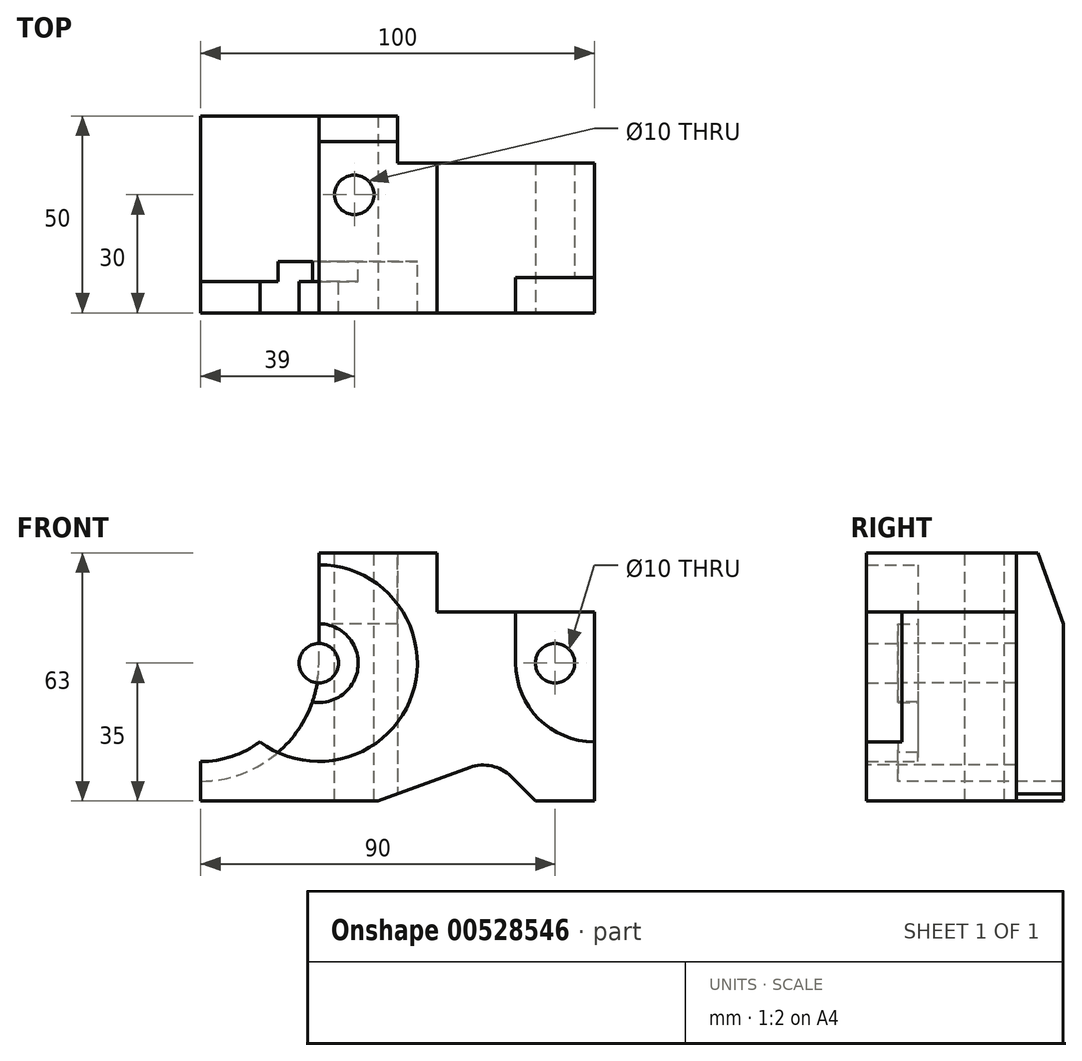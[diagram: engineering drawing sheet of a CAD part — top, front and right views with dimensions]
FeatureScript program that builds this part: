
annotation { "Feature Type Name" : "Feature", "Feature Type Description" : "" }
export const myFeature = defineFeature(function(context is Context, id is Id, definition is map)
    precondition{}
    {
        {
            var Q0;
            Q0=qCreatedBy(makeId("Front.planeOp"),FACE);
            var sketch = newSketch(context, id + "F0", { "sketchPlane" : qUnion([Q0])});
            skLineSegment(sketch, "E0", {"start": v(0, 0) * mm, "end": v(-15, 0) * mm});
            skLineSegment(sketch, "E1", {"start": v(-100, 0) * mm, "end": v(-100, 63) * mm});
            skLineSegment(sketch, "E2", {"start": v(-100, 63) * mm, "end": v(-40, 63) * mm});
            skLineSegment(sketch, "E3", {"start": v(-40, 63) * mm, "end": v(-40, 48) * mm});
            skLineSegment(sketch, "E4", {"start": v(-40, 48) * mm, "end": v(0, 48) * mm});
            skLineSegment(sketch, "E5", {"start": v(0, 48) * mm, "end": v(0, 0) * mm});
            skLineSegment(sketch, "E6", {"start": v(-15, 0) * mm, "end": v(-21.17, 6.17) * mm});
            skArc(sketch, "E7", {"start": v(-21.17, 6.17) * mm, "mid": v(-26.08, 8.86) * mm, "end": v(-31.66, 8.5) * mm});
            skLineSegment(sketch, "E8", {"start": v(-31.66, 8.5) * mm, "end": v(-55, 0) * mm});
            skLineSegment(sketch, "E9.trimOffspring", {"start": v(-55, 0) * mm, "end": v(-100, 0) * mm});
            skSolve(sketch);
        }
        {
            var Q0;
            Q0 = qSketchRegion(id + "F0", true);
            extrude(context, id + "F1", {"entities" : qUnion([Q0]), "oppositeDirection" : true, "depth" : 50 * mm, "offsetDistance" : 25 * mm});
        }
        {
            var Q0;
            Q0=qCreatedBy(makeId("Top.planeOp"),FACE);
            cPlane(context, id + "F2", {"entities" : qUnion([Q0]), "cplaneType" : CPlaneType.OFFSET, "offset" : 35 * mm, "width" : 150 * mm, "height" : 150 * mm});
        }
        {
            var Q0;
            Q0=qCreatedBy(id+"F2.planeOp",FACE);
            var sketch = newSketch(context, id + "F3", { "sketchPlane" : qUnion([Q0])});
            skLineSegment(sketch, "E10", {"start": v(-70, -45.38) * mm, "end": v(-70, 0) * mm});
            skLineSegment(sketch, "E11", {"start": v(-70, 0) * mm, "end": v(-75, 0) * mm});
            skLineSegment(sketch, "E12", {"start": v(-75, 0) * mm, "end": v(-75, 8) * mm});
            skLineSegment(sketch, "E13", {"start": v(-75, 8) * mm, "end": v(-80, 8) * mm});
            skLineSegment(sketch, "E14", {"start": v(-95, 13) * mm, "end": v(-95, -45.38) * mm});
            skLineSegment(sketch, "E15", {"start": v(-95, -45.38) * mm, "end": v(-70, -45.38) * mm});
            skLineSegment(sketch, "E16", {"start": v(-80, 8) * mm, "end": v(-80, 13) * mm});
            skLineSegment(sketch, "E17", {"start": v(-80, 13) * mm, "end": v(-95, 13) * mm});
            skLineSegment(sketch, "E18", {"start": v(-70, 0) * mm, "end": v(-70, 92.14) * mm, "construction": true});
            skSolve(sketch);
        }
        {
            var Q0;
            Q0=makeQuery(id+"F3.imprint","IMPRINT",FACE,{"disambiguationData":[TD([[makeQuery(id+"F3.imprint","IMPRINT",EDGE,{"derivedFrom":sQuery(id+"F3.wireOp",EDGE,"E10")}),1.0]])]});
            var Q1;
            Q1=sQuery(id+"F3.wireOp",EDGE,"E18");
            revolve(context, id + "F4", {"operationType" : NewBodyOperationType.REMOVE, "entities" : qUnion([Q0]), "axis" : qUnion([Q1]), "revolveType" : RevolveType.FULL, "oppositeDirection" : true});
        }
        {
            var Q0;
            Q0=qCreatedBy(makeId("Front.planeOp"),FACE);
            var sketch = newSketch(context, id + "F5", { "sketchPlane" : qUnion([Q0])});
            skLineSegment(sketch, "E19", {"start": v(-20, 71.47) * mm, "end": v(-20, 35) * mm});
            skArc(sketch, "E20", {"start": v(-20, 35) * mm, "mid": v(-14.14, 20.86) * mm, "end": v(0, 15) * mm});
            skLineSegment(sketch, "E21", {"start": v(0, 15) * mm, "end": v(24.4, 15) * mm});
            skLineSegment(sketch, "E22", {"start": v(-20, 71.47) * mm, "end": v(24.4, 71.47) * mm});
            skLineSegment(sketch, "E23", {"start": v(24.4, 71.47) * mm, "end": v(24.4, 15) * mm});
            skCircle(sketch, "E24.0.0", {"center": v(-70, 35) * mm, "radius": 5 * mm, "construction": true});
            skLineSegment(sketch, "E25", {"start": v(-70, 35) * mm, "end": v(0, 35) * mm, "construction": true});
            skSolve(sketch);
        }
        {
            var Q0;
            Q0 = qSketchRegion(id + "F5", true);
            extrude(context, id + "F6", {"entities" : qUnion([Q0]), "operationType" : NewBodyOperationType.REMOVE, "oppositeDirection" : true, "depth" : 9 * mm, "offsetDistance" : 25 * mm});
        }
        {
            var Q0;
            Q0=qCreatedBy(makeId("Front.planeOp"),FACE);
            var sketch = newSketch(context, id + "F7", { "sketchPlane" : qUnion([Q0])});
            skCircle(sketch, "E26", {"center": v(-10, 35) * mm, "radius": 5 * mm});
            skSolve(sketch);
        }
        {
            var Q0;
            Q0 = qSketchRegion(id + "F7", true);
            extrude(context, id + "F8", {"entities" : qUnion([Q0]), "operationType" : NewBodyOperationType.REMOVE, "endBound" : BoundingType.THROUGH_ALL, "oppositeDirection" : true, "depth" : 25 * mm, "offsetDistance" : 25 * mm});
        }
        {
            var Q0;
            Q0=qCreatedBy(makeId("Front.planeOp"),FACE);
            cPlane(context, id + "F9", {"entities" : qUnion([Q0]), "cplaneType" : CPlaneType.OFFSET, "offset" : 8 * mm, "oppositeDirection" : true, "width" : 150 * mm, "height" : 150 * mm});
        }
        {
            var Q0;
            Q0=qCreatedBy(id+"F9.planeOp",FACE);
            var sketch = newSketch(context, id + "F10", { "sketchPlane" : qUnion([Q0])});
            skLineSegment(sketch, "E27", {"start": v(-192.21, 5) * mm, "end": v(-100, 5) * mm});
            skLineSegment(sketch, "E28", {"start": v(-70, 35) * mm, "end": v(-70, 107.14) * mm});
            skLineSegment(sketch, "E29", {"start": v(-70, 107.14) * mm, "end": v(-192.21, 107.14) * mm});
            skLineSegment(sketch, "E30", {"start": v(-192.21, 107.14) * mm, "end": v(-192.21, 5) * mm});
            skPoint(sketch, "E31.visualSharp", {"position": v(-70, 5) * mm});
            skArc(sketch, "E31.filletArc", {"start": v(-100, 5) * mm, "mid": v(-78.79, 13.79) * mm, "end": v(-70, 35) * mm});
            skSolve(sketch);
        }
        {
            var Q0;
            Q0 = qSketchRegion(id + "F10", true);
            extrude(context, id + "F11", {"entities" : qUnion([Q0]), "operationType" : NewBodyOperationType.REMOVE, "endBound" : BoundingType.THROUGH_ALL, "oppositeDirection" : true, "depth" : 25 * mm, "offsetDistance" : 25 * mm});
        }
        {
            var Q0;
            Q0=qCreatedBy(id+"F9.planeOp",FACE);
            var sketch = newSketch(context, id + "F12", { "sketchPlane" : qUnion([Q0])});
            skLineSegment(sketch, "E32", {"start": v(-100, 14.4) * mm, "end": v(-100, 35) * mm, "construction": true});
            skLineSegment(sketch, "E33", {"start": v(-100, 35) * mm, "end": v(-70, 35) * mm, "construction": true});
            skArc(sketch, "E34", {"start": v(-123.4, 26.22) * mm, "mid": v(-95.54, 10.4) * mm, "end": v(-75, 35) * mm});
            skLineSegment(sketch, "E35", {"start": v(-75, 35) * mm, "end": v(-75, 45) * mm});
            skLineSegment(sketch, "E36", {"start": v(-75, 45) * mm, "end": v(-70, 45) * mm});
            skLineSegment(sketch, "E37", {"start": v(-70, 45) * mm, "end": v(-70, 99.63) * mm});
            skLineSegment(sketch, "E38", {"start": v(-70, 99.63) * mm, "end": v(-123.4, 99.63) * mm});
            skLineSegment(sketch, "E39", {"start": v(-123.4, 99.63) * mm, "end": v(-123.4, 26.22) * mm});
            skSolve(sketch);
        }
        {
            var Q0;
            Q0 = qSketchRegion(id + "F12", true);
            extrude(context, id + "F13", {"entities" : qUnion([Q0]), "operationType" : NewBodyOperationType.REMOVE, "depth" : 25 * mm, "offsetDistance" : 25 * mm});
        }
        {
            var Q0;
            Q0=makeQuery(id+"F13.boolean.opBoolean","MERGE",FACE,{"derivedFrom":[makeQuery(id+"F11.boolean.opBoolean","COPY",FACE,{"derivedFrom":makeQuery(id+"F11.opExtrude","SWEPT_FACE",FACE,{"disambiguationData":[OSD([sQuery(id+"F10.wireOp",EDGE,"E28")])]})}),makeQuery(id+"F13.opExtrude","SWEPT_FACE",FACE,{"disambiguationData":[OSD([sQuery(id+"F12.wireOp",EDGE,"E37")])]})]});
            var sketch = newSketch(context, id + "F14", { "sketchPlane" : qUnion([Q0])});
            skLineSegment(sketch, "E40", {"start": v(-50, 63) * mm, "end": v(-50, 45) * mm});
            skLineSegment(sketch, "E41", {"start": v(-50, 45) * mm, "end": v(-43.45, 63) * mm});
            skLineSegment(sketch, "E42", {"start": v(-43.45, 63) * mm, "end": v(-50, 63) * mm});
            skSolve(sketch);
        }
        {
            var Q0;
            Q0 = qSketchRegion(id + "F14", true);
            extrude(context, id + "F15", {"entities" : qUnion([Q0]), "operationType" : NewBodyOperationType.REMOVE, "endBound" : BoundingType.THROUGH_ALL, "oppositeDirection" : true, "depth" : 25 * mm, "offsetDistance" : 25 * mm});
        }
        {
            var Q0;
            Q0=makeQuery(id+"F1.opExtrude","SWEPT_FACE",FACE,{"disambiguationData":[OSD([sQuery(id+"F0.wireOp",EDGE,"E2")])]});
            var sketch = newSketch(context, id + "F16", { "sketchPlane" : qUnion([Q0])});
            skCircle(sketch, "E43", {"center": v(-61, 30) * mm, "radius": 5 * mm});
            skSolve(sketch);
        }
        {
            var Q0;
            Q0 = qSketchRegion(id + "F16", true);
            extrude(context, id + "F17", {"entities" : qUnion([Q0]), "operationType" : NewBodyOperationType.REMOVE, "endBound" : BoundingType.THROUGH_ALL, "oppositeDirection" : true, "depth" : 25 * mm, "offsetDistance" : 25 * mm});
        }
        {
            var Q0;
            Q0=qCreatedBy(makeId("Top.planeOp"),FACE);
            var sketch = newSketch(context, id + "F18", { "sketchPlane" : qUnion([Q0])});
            skLineSegment(sketch, "E44.bottom", {"start": v(0, 50) * mm, "end": v(-50, 50) * mm});
            skLineSegment(sketch, "E44.top", {"start": v(0, 38) * mm, "end": v(-50, 38) * mm});
            skLineSegment(sketch, "E44.left", {"start": v(0, 50) * mm, "end": v(0, 38) * mm});
            skLineSegment(sketch, "E44.right", {"start": v(-50, 50) * mm, "end": v(-50, 38) * mm});
            skSolve(sketch);
        }
        {
            var Q0;
            Q0 = qSketchRegion(id + "F18", true);
            extrude(context, id + "F19", {"entities" : qUnion([Q0]), "operationType" : NewBodyOperationType.REMOVE, "endBound" : BoundingType.THROUGH_ALL, "depth" : 25 * mm, "offsetDistance" : 25 * mm});
        }
    });
